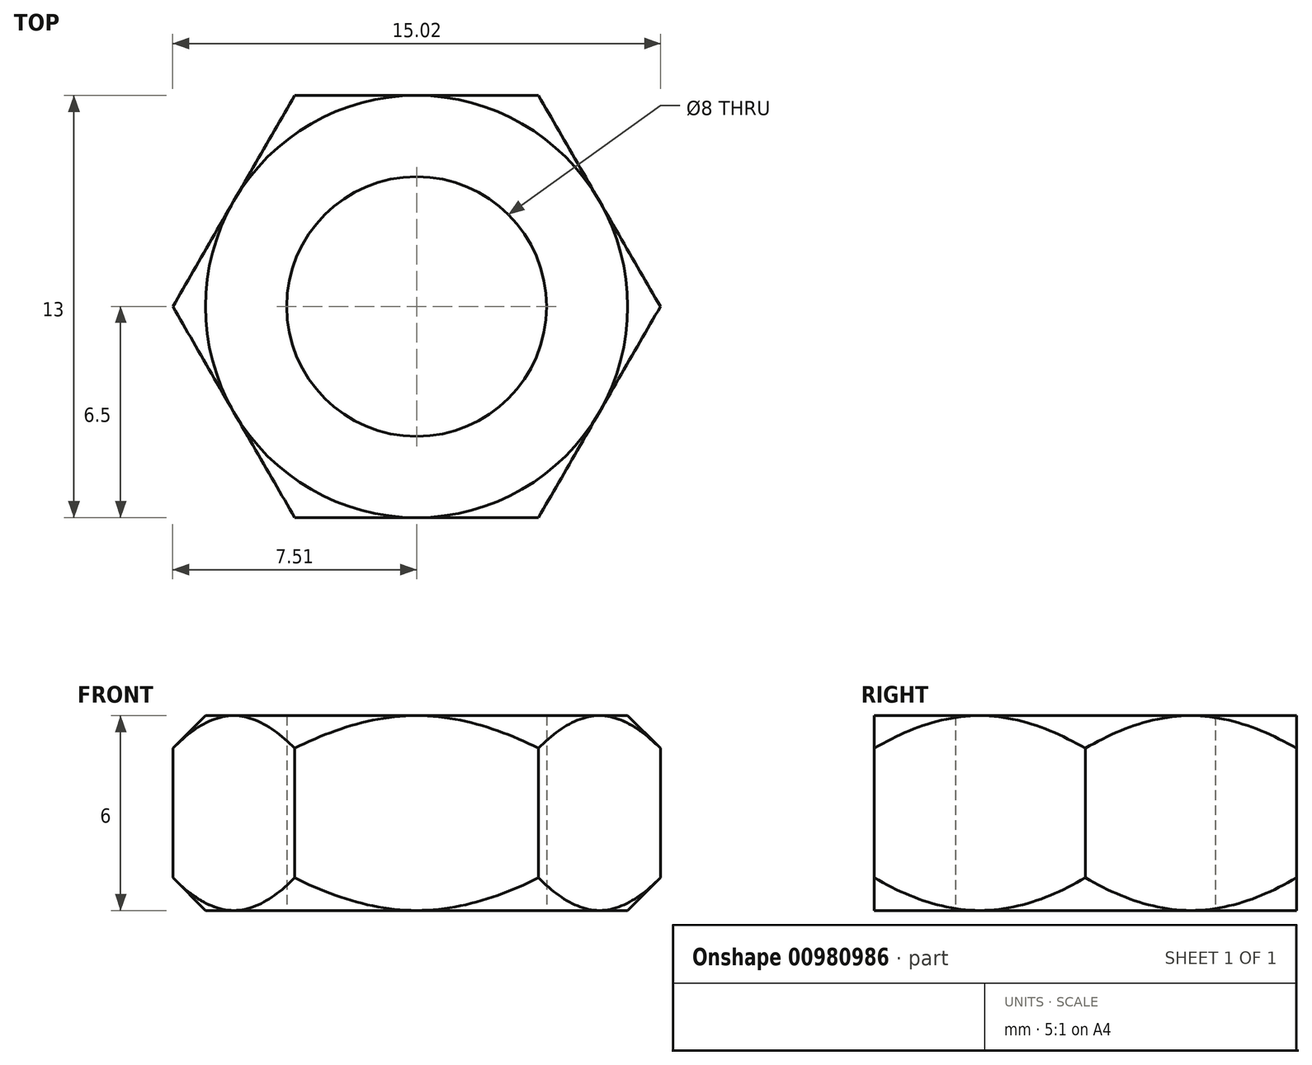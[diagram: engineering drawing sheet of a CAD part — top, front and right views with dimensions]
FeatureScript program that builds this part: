
annotation { "Feature Type Name" : "Feature", "Feature Type Description" : "" }
export const myFeature = defineFeature(function(context is Context, id is Id, definition is map)
    precondition{}
    {
        {
            var Q0;
            Q0=qCreatedBy(makeId("Top.planeOp"),FACE);
            var sketch = newSketch(context, id + "F0", { "sketchPlane" : qUnion([Q0])});
            skCircle(sketch, "E0.cCircle", {"center": v(0, 0) * mm, "radius": 6.5 * mm, "construction": true});
            skLineSegment(sketch, "E0.0", {"start": v(-3.75, 6.5) * mm, "end": v(3.75, 6.5) * mm});
            skLineSegment(sketch, "E0.1", {"start": v(3.75, 6.5) * mm, "end": v(7.5, 0) * mm});
            skLineSegment(sketch, "E0.2", {"start": v(7.5, 0) * mm, "end": v(3.75, -6.5) * mm});
            skLineSegment(sketch, "E0.3", {"start": v(3.75, -6.5) * mm, "end": v(-3.75, -6.5) * mm});
            skLineSegment(sketch, "E0.4", {"start": v(-3.75, -6.5) * mm, "end": v(-7.5, 0) * mm});
            skLineSegment(sketch, "E0.5", {"start": v(-7.5, 0) * mm, "end": v(-3.75, 6.5) * mm});
            skPoint(sketch, "E0.0.midPoint", {"position": v(0, 6.5) * mm});
            skCircle(sketch, "E1", {"center": v(0, 0) * mm, "radius": 4 * mm});
            skSolve(sketch);
        }
        {
            var Q0;
            Q0=makeQuery(id+"F0.imprint","IMPRINT",FACE,{"disambiguationData":[TD([[makeQuery(id+"F0.imprint","IMPRINT",EDGE,{"derivedFrom":sQuery(id+"F0.wireOp",EDGE,"E0.0")}),-1.0]])]});
            extrude(context, id + "F1", {"entities" : qUnion([Q0]), "depth" : 6 * mm, "offsetDistance" : 25 * mm});
        }
        {
            var Q0;
            Q0=qCreatedBy(makeId("Front.planeOp"),FACE);
            var sketch = newSketch(context, id + "F2", { "sketchPlane" : qUnion([Q0])});
            skLineSegment(sketch, "E2", {"start": v(0, -5.5) * mm, "end": v(0, 13.93) * mm, "construction": true});
            skLineSegment(sketch, "E3", {"start": v(-7.55, 4.95) * mm, "end": v(-6.5, 6) * mm});
            skLineSegment(sketch, "E4", {"start": v(-6.5, 6) * mm, "end": v(-7.55, 6) * mm});
            skLineSegment(sketch, "E5", {"start": v(-7.55, 6) * mm, "end": v(-7.55, 4.95) * mm});
            skLineSegment(sketch, "E6", {"start": v(-7.55, 1.05) * mm, "end": v(-7.55, 0) * mm});
            skLineSegment(sketch, "E7", {"start": v(-7.55, 0) * mm, "end": v(-6.5, 0) * mm});
            skLineSegment(sketch, "E8", {"start": v(-6.5, 0) * mm, "end": v(-7.55, 1.05) * mm});
            skSolve(sketch);
        }
        {
            var Q0;
            Q0=makeQuery(id+"F2.imprint","IMPRINT",FACE,{"disambiguationData":[TD([[makeQuery(id+"F2.imprint","IMPRINT",EDGE,{"derivedFrom":sQuery(id+"F2.wireOp",EDGE,"E3")}),1.0]])]});
            var Q1;
            Q1=makeQuery(id+"F2.imprint","IMPRINT",FACE,{"disambiguationData":[TD([[makeQuery(id+"F2.imprint","IMPRINT",EDGE,{"derivedFrom":sQuery(id+"F2.wireOp",EDGE,"E6")}),1.0]])]});
            var Q2;
            Q2=sQuery(id+"F2.wireOp",EDGE,"E2");
            revolve(context, id + "F3", {"operationType" : NewBodyOperationType.REMOVE, "surfaceOperationType" : NewSurfaceOperationType.NEW, "entities" : qUnion([Q0, Q1]), "axis" : qUnion([Q2]), "revolveType" : RevolveType.FULL, "oppositeDirection" : true});
        }
    });
